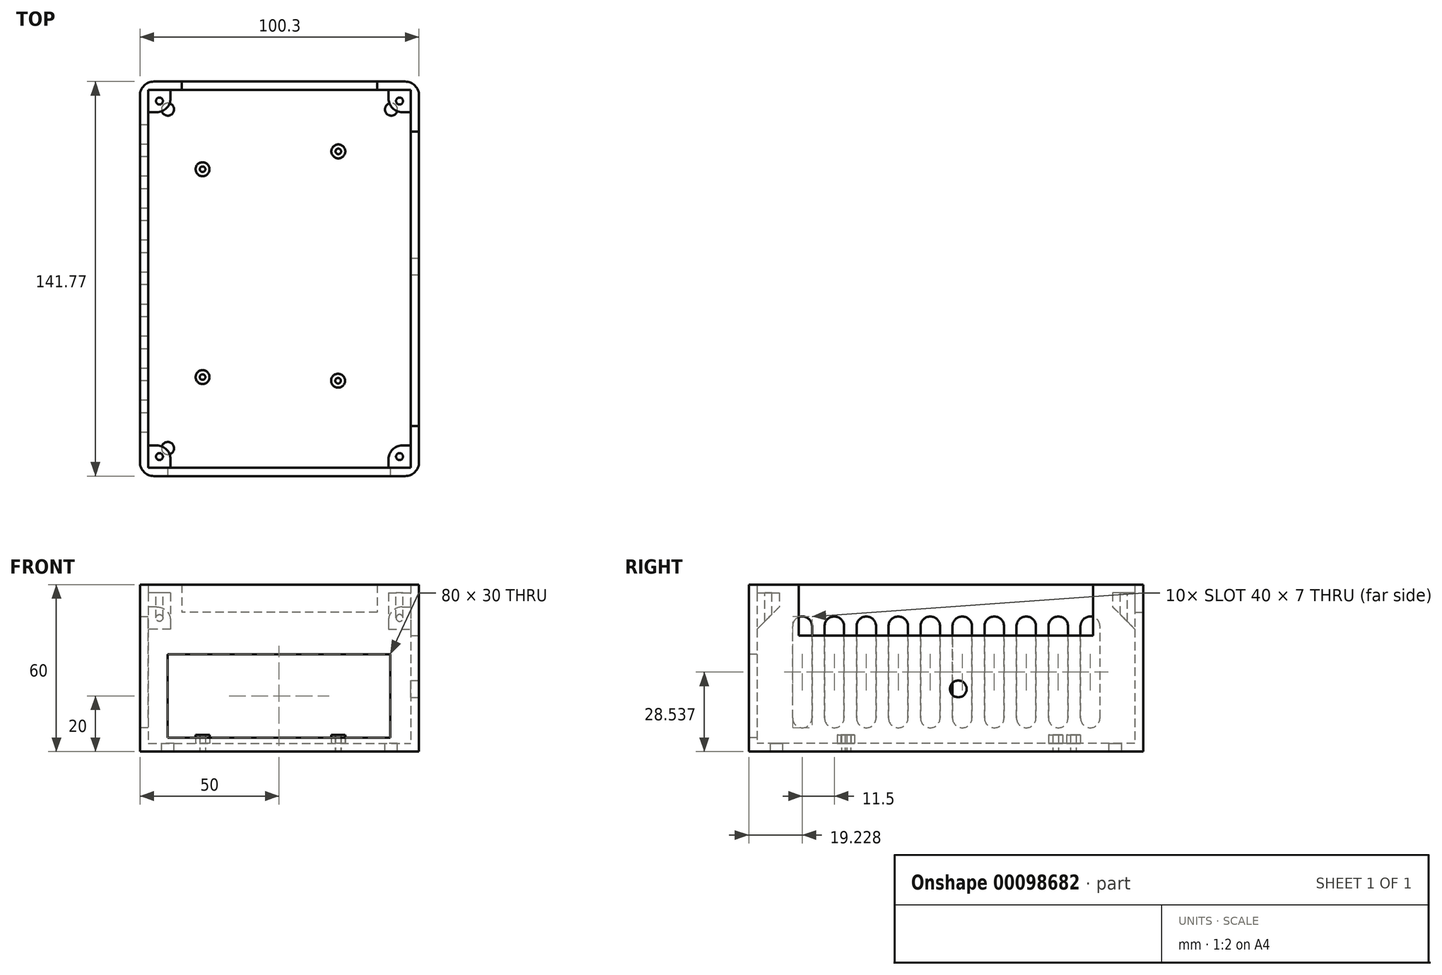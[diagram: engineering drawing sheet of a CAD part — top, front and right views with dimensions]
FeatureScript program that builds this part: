
annotation { "Feature Type Name" : "Feature", "Feature Type Description" : "" }
export const myFeature = defineFeature(function(context is Context, id is Id, definition is map)
    precondition{}
    {
        {
            var Q0;
            Q0=qCreatedBy(makeId("Top.planeOp"),FACE);
            var sketch = newSketch(context, id + "F0", { "sketchPlane" : qUnion([Q0])});
            skLineSegment(sketch, "E0.bottom", {"start": v(-36.7, -58.9) * mm, "end": v(23.6, -58.9) * mm});
            skLineSegment(sketch, "E0.top", {"start": v(-36.7, 42.88) * mm, "end": v(23.6, 42.88) * mm});
            skLineSegment(sketch, "E0.left", {"start": v(-36.7, -58.9) * mm, "end": v(-36.7, 42.88) * mm});
            skLineSegment(sketch, "E0.right", {"start": v(23.6, -58.9) * mm, "end": v(23.6, 42.88) * mm});
            skCircle(sketch, "E1", {"center": v(-34.2, 31.38) * mm, "radius": 2 * mm});
            skCircle(sketch, "E2", {"center": v(14.6, 37.78) * mm, "radius": 2 * mm});
            skCircle(sketch, "E3", {"center": v(-18.03, 7.58) * mm, "radius": 2 * mm});
            skCircle(sketch, "E4", {"center": v(9.3, 7.58) * mm, "radius": 2 * mm});
            skCircle(sketch, "E5", {"center": v(-34.2, -43.32) * mm, "radius": 2 * mm});
            skCircle(sketch, "E6", {"center": v(14.5, -44.62) * mm, "radius": 2 * mm});
            skSolve(sketch);
        }
        {
            var Q0;
            Q0=makeQuery(id+"F0.imprint","IMPRINT",FACE,{"disambiguationData":[TD([[makeQuery(id+"F0.imprint","IMPRINT",EDGE,{"derivedFrom":sQuery(id+"F0.wireOp",EDGE,"E0.bottom")}),1.0]])]});
            var sketch = newSketch(context, id + "F1", { "sketchPlane" : qUnion([Q0])});
            skLineSegment(sketch, "E7.bottom", {"start": v(-56.7, 62.88) * mm, "end": v(43.6, 62.88) * mm});
            skLineSegment(sketch, "E7.top", {"start": v(-56.7, -78.9) * mm, "end": v(43.6, -78.9) * mm});
            skLineSegment(sketch, "E7.left", {"start": v(-56.7, 62.88) * mm, "end": v(-56.7, -78.9) * mm});
            skLineSegment(sketch, "E7.right", {"start": v(43.6, 62.88) * mm, "end": v(43.6, -78.9) * mm});
            skSolve(sketch);
        }
        {
            var Q0;
            Q0 = qSketchRegion(id + "F1", true);
            extrude(context, id + "F2", {"entities" : qUnion([Q0]), "depth" : 60 * mm});
        }
        {
            var Q0;
            Q0=makeQuery(id+"F2.opExtrude","CAP_FACE",FACE,{"disambiguationData":[OSD([sQuery(id+"F1.wireOp",EDGE,"E7.bottom"),sQuery(id+"F1.wireOp",EDGE,"E7.top"),sQuery(id+"F1.wireOp",EDGE,"E7.left"),sQuery(id+"F1.wireOp",EDGE,"E7.right")])],"isStart":false});
            shell(context, id + "F3", {"entities" : qUnion([Q0]), "thickness" : 3 * mm});
        }
        {
            var Q0;
            Q0=makeQuery(id+"F3.opShell","OFFSET_FACE",FACE,{"disambiguationData":[OSD([sQuery(id+"F1.wireOp",EDGE,"E7.bottom"),sQuery(id+"F1.wireOp",EDGE,"E7.top"),sQuery(id+"F1.wireOp",EDGE,"E7.left"),sQuery(id+"F1.wireOp",EDGE,"E7.right")])]});
            var sketch = newSketch(context, id + "F4", { "sketchPlane" : qUnion([Q0])});
            skCircle(sketch, "E8.0", {"center": v(-34.2, 31.38) * mm, "radius": 2 * mm});
            skCircle(sketch, "E9.0", {"center": v(14.6, 37.78) * mm, "radius": 2 * mm});
            skCircle(sketch, "E10.0", {"center": v(-34.2, -43.32) * mm, "radius": 2 * mm});
            skCircle(sketch, "E11.0", {"center": v(14.5, -44.62) * mm, "radius": 2 * mm});
            skSolve(sketch);
        }
        {
            var Q0;
            Q0=makeQuery(id+"F4.imprint","IMPRINT",FACE,{"disambiguationData":[TD([[makeQuery(id+"F4.imprint","IMPRINT",EDGE,{"derivedFrom":sQuery(id+"F4.wireOp",EDGE,"E8.0")}),1.0]])]});
            var Q1;
            Q1=makeQuery(id+"F4.imprint","IMPRINT",FACE,{"disambiguationData":[TD([[makeQuery(id+"F4.imprint","IMPRINT",EDGE,{"derivedFrom":sQuery(id+"F4.wireOp",EDGE,"E9.0")}),1.0]])]});
            var Q2;
            Q2=makeQuery(id+"F4.imprint","IMPRINT",FACE,{"disambiguationData":[TD([[makeQuery(id+"F4.imprint","IMPRINT",EDGE,{"derivedFrom":sQuery(id+"F4.wireOp",EDGE,"E11.0")}),1.0]])]});
            var Q3;
            Q3=makeQuery(id+"F4.imprint","IMPRINT",FACE,{"disambiguationData":[TD([[makeQuery(id+"F4.imprint","IMPRINT",EDGE,{"derivedFrom":sQuery(id+"F4.wireOp",EDGE,"E10.0")}),1.0]])]});
            extrude(context, id + "F5", {"entities" : qUnion([Q0, Q1, Q2, Q3]), "operationType" : NewBodyOperationType.REMOVE, "oppositeDirection" : true, "depth" : 25 * mm});
        }
        {
            var Q0;
            Q0=makeQuery(id+"F2.opExtrude","SWEPT_FACE",FACE,{"disambiguationData":[OSD([sQuery(id+"F1.wireOp",EDGE,"E7.top")])]});
            var sketch = newSketch(context, id + "F6", { "sketchPlane" : qUnion([Q0])});
            skLineSegment(sketch, "E12.bottom", {"start": v(33.3, 5) * mm, "end": v(-46.7, 5) * mm});
            skLineSegment(sketch, "E12.top", {"start": v(33.3, 35) * mm, "end": v(-46.7, 35) * mm});
            skLineSegment(sketch, "E12.left", {"start": v(33.3, 5) * mm, "end": v(33.3, 35) * mm});
            skLineSegment(sketch, "E12.right", {"start": v(-46.7, 5) * mm, "end": v(-46.7, 35) * mm});
            skPoint(sketch, "E12.middle", {"position": v(-6.7, 20) * mm});
            skSolve(sketch);
        }
        {
            var Q0;
            Q0 = qSketchRegion(id + "F6", true);
            extrude(context, id + "F7", {"entities" : qUnion([Q0]), "operationType" : NewBodyOperationType.REMOVE, "oppositeDirection" : true, "depth" : 25 * mm});
        }
        {
            var Q0;
            Q0=makeQuery(id+"F2.opExtrude","SWEPT_FACE",FACE,{"disambiguationData":[OSD([sQuery(id+"F1.wireOp",EDGE,"E7.right")])]});
            var sketch = newSketch(context, id + "F8", { "sketchPlane" : qUnion([Q0])});
            skLineSegment(sketch, "E13.bottom", {"start": v(-60.9, 60) * mm, "end": v(44.88, 60) * mm});
            skLineSegment(sketch, "E13.top", {"start": v(-60.9, 41.64) * mm, "end": v(44.88, 41.64) * mm});
            skLineSegment(sketch, "E13.left", {"start": v(-60.9, 60) * mm, "end": v(-60.9, 41.64) * mm});
            skLineSegment(sketch, "E13.right", {"start": v(44.88, 60) * mm, "end": v(44.88, 41.64) * mm});
            skSolve(sketch);
        }
        {
            var Q0;
            Q0 = qSketchRegion(id + "F8", true);
            extrude(context, id + "F9", {"entities" : qUnion([Q0]), "operationType" : NewBodyOperationType.REMOVE, "oppositeDirection" : true, "depth" : 25 * mm});
        }
        {
            var Q0;
            Q0=makeQuery(id+"F2.opExtrude","SWEPT_FACE",FACE,{"disambiguationData":[OSD([sQuery(id+"F1.wireOp",EDGE,"E7.bottom")])]});
            var sketch = newSketch(context, id + "F10", { "sketchPlane" : qUnion([Q0])});
            skLineSegment(sketch, "E14.bottom", {"start": v(-28.6, 60) * mm, "end": v(41.7, 60) * mm});
            skLineSegment(sketch, "E14.top", {"start": v(-28.6, 50) * mm, "end": v(41.7, 50) * mm});
            skLineSegment(sketch, "E14.left", {"start": v(-28.6, 60) * mm, "end": v(-28.6, 50) * mm});
            skLineSegment(sketch, "E14.right", {"start": v(41.7, 60) * mm, "end": v(41.7, 50) * mm});
            skSolve(sketch);
        }
        {
            var Q0;
            Q0 = qSketchRegion(id + "F10", true);
            extrude(context, id + "F11", {"entities" : qUnion([Q0]), "operationType" : NewBodyOperationType.REMOVE, "oppositeDirection" : true, "depth" : 25 * mm});
        }
        {
            var Q0;
            Q0=makeQuery(id+"F3.opShell","OFFSET_FACE",FACE,{"disambiguationData":[OSD([sQuery(id+"F1.wireOp",EDGE,"E7.bottom"),sQuery(id+"F1.wireOp",EDGE,"E7.top"),sQuery(id+"F1.wireOp",EDGE,"E7.left"),sQuery(id+"F1.wireOp",EDGE,"E7.right")])]});
            var sketch = newSketch(context, id + "F12", { "sketchPlane" : qUnion([Q0])});
            skLineSegment(sketch, "E15.bottom", {"start": v(-46.7, 52.88) * mm, "end": v(33.6, 52.88) * mm, "construction": true});
            skLineSegment(sketch, "E15.top", {"start": v(-46.7, -68.9) * mm, "end": v(33.6, -68.9) * mm, "construction": true});
            skLineSegment(sketch, "E15.left", {"start": v(-46.7, 52.88) * mm, "end": v(-46.7, -68.9) * mm, "construction": true});
            skLineSegment(sketch, "E15.right", {"start": v(33.6, 52.88) * mm, "end": v(33.6, -68.9) * mm, "construction": true});
            skPoint(sketch, "E15.middle", {"position": v(-6.55, -8) * mm});
            skPoint(sketch, "E15.middle.positionSnap0", {"position": v(-53.7, -8) * mm});
            skPoint(sketch, "E15.middle.positionSnap1", {"position": v(-6.55, 59.88) * mm});
            skPoint(sketch, "E15.centerSnap0", {"position": v(-53.7, -8) * mm});
            skPoint(sketch, "E15.centerSnap1", {"position": v(-6.55, 59.88) * mm});
            skCircle(sketch, "E16", {"center": v(-46.7, 52.88) * mm, "radius": 2.25 * mm});
            skCircle(sketch, "E17", {"center": v(33.6, 52.88) * mm, "radius": 2.25 * mm});
            skCircle(sketch, "E18", {"center": v(-46.7, -68.9) * mm, "radius": 2.25 * mm});
            skSolve(sketch);
        }
        {
            var Q0;
            Q0 = qSketchRegion(id + "F12", true);
            extrude(context, id + "F13", {"entities" : qUnion([Q0]), "operationType" : NewBodyOperationType.REMOVE, "oppositeDirection" : true, "depth" : 25 * mm});
        }
        {
            var Q0;
            Q0=makeQuery(id+"F3.opShell","OFFSET_FACE",FACE,{"disambiguationData":[OSD([sQuery(id+"F1.wireOp",EDGE,"E7.left")])]});
            var sketch = newSketch(context, id + "F14", { "sketchPlane" : qUnion([Q0])});
            skLineSegment(sketch, "E19", {"start": v(59.88, 57) * mm, "end": v(51.88, 57) * mm});
            skLineSegment(sketch, "E20", {"start": v(51.88, 57) * mm, "end": v(51.88, 52) * mm});
            skLineSegment(sketch, "E21", {"start": v(51.88, 52) * mm, "end": v(59.88, 44) * mm});
            skLineSegment(sketch, "E22", {"start": v(59.88, 44) * mm, "end": v(59.88, 57) * mm});
            skLineSegment(sketch, "E23", {"start": v(-8, 60) * mm, "end": v(-8, 44.9) * mm});
            skPoint(sketch, "E23.endSnap0", {"position": v(-8, 60) * mm});
            skLineSegment(sketch, "E24.MirrorCS", {"start": v(-75.9, 44) * mm, "end": v(-75.9, 57) * mm});
            skLineSegment(sketch, "E25.MirrorCS", {"start": v(-75.9, 57) * mm, "end": v(-67.9, 57) * mm});
            skLineSegment(sketch, "E26.MirrorCS", {"start": v(-67.9, 52) * mm, "end": v(-75.9, 44) * mm});
            skLineSegment(sketch, "E27.MirrorCS", {"start": v(-67.9, 57) * mm, "end": v(-67.9, 52) * mm});
            skSolve(sketch);
        }
        {
            var Q0;
            Q0 = qSketchRegion(id + "F14", true);
            extrude(context, id + "F15", {"entities" : qUnion([Q0]), "operationType" : NewBodyOperationType.ADD, "depth" : 8 * mm});
        }
        {
            var Q0;
            Q0=makeQuery(id+"F3.opShell","OFFSET_FACE",FACE,{"disambiguationData":[OSD([sQuery(id+"F1.wireOp",EDGE,"E7.right")])]});
            var sketch = newSketch(context, id + "F16", { "sketchPlane" : qUnion([Q0])});
            skLineSegment(sketch, "E28.0.0", {"start": v(-59.88, 44) * mm, "end": v(-59.88, 57) * mm});
            skLineSegment(sketch, "E28.0.1", {"start": v(-59.88, 57) * mm, "end": v(-51.88, 57) * mm});
            skLineSegment(sketch, "E28.0.2", {"start": v(-51.88, 57) * mm, "end": v(-51.88, 52) * mm});
            skLineSegment(sketch, "E28.0.3", {"start": v(-51.88, 52) * mm, "end": v(-59.88, 44) * mm});
            skLineSegment(sketch, "E29.0.0", {"start": v(67.9, 57) * mm, "end": v(75.9, 57) * mm});
            skLineSegment(sketch, "E29.0.1", {"start": v(75.9, 57) * mm, "end": v(75.9, 44) * mm});
            skLineSegment(sketch, "E29.0.2", {"start": v(75.9, 44) * mm, "end": v(67.9, 52) * mm});
            skLineSegment(sketch, "E29.0.3", {"start": v(67.9, 52) * mm, "end": v(67.9, 57) * mm});
            skSolve(sketch);
        }
        {
            var Q0;
            Q0 = qSketchRegion(id + "F16", true);
            extrude(context, id + "F17", {"entities" : qUnion([Q0]), "operationType" : NewBodyOperationType.ADD, "depth" : 8 * mm});
        }
        {
            var Q0;
            Q0=makeQuery(id+"F17.opExtrude","SWEPT_FACE",FACE,{"disambiguationData":[OSD([sQuery(id+"F16.wireOp",EDGE,"E28.0.1")])]});
            var sketch = newSketch(context, id + "F18", { "sketchPlane" : qUnion([Q0])});
            skCircle(sketch, "E30", {"center": v(36.6, 55.88) * mm, "radius": 1.25 * mm});
            skPoint(sketch, "E30.centerSnap0", {"position": v(36.6, 59.88) * mm});
            skPoint(sketch, "E31", {"position": v(32.6, 55.88) * mm});
            skSolve(sketch);
        }
        {
            var Q0;
            Q0=makeQuery(id+"F15.opExtrude","SWEPT_FACE",FACE,{"disambiguationData":[OSD([sQuery(id+"F14.wireOp",EDGE,"E19")])]});
            var sketch = newSketch(context, id + "F19", { "sketchPlane" : qUnion([Q0])});
            skCircle(sketch, "E32", {"center": v(-49.7, 55.88) * mm, "radius": 1.25 * mm});
            skPoint(sketch, "E32.centerSnap0", {"position": v(-45.7, 55.88) * mm});
            skPoint(sketch, "E32.centerSnap1", {"position": v(-49.7, 51.88) * mm});
            skSolve(sketch);
        }
        {
            var Q0;
            Q0=makeQuery(id+"F15.opExtrude","SWEPT_FACE",FACE,{"disambiguationData":[OSD([sQuery(id+"F14.wireOp",EDGE,"E25.MirrorCS")])]});
            var sketch = newSketch(context, id + "F20", { "sketchPlane" : qUnion([Q0])});
            skCircle(sketch, "E33", {"center": v(-49.7, -71.9) * mm, "radius": 1.25 * mm});
            skPoint(sketch, "E33.centerSnap0", {"position": v(-45.7, -71.9) * mm});
            skPoint(sketch, "E33.centerSnap1", {"position": v(-49.7, -67.9) * mm});
            skSolve(sketch);
        }
        {
            var Q0;
            Q0=makeQuery(id+"F17.opExtrude","SWEPT_FACE",FACE,{"disambiguationData":[OSD([sQuery(id+"F16.wireOp",EDGE,"E29.0.0")])]});
            var sketch = newSketch(context, id + "F21", { "sketchPlane" : qUnion([Q0])});
            skCircle(sketch, "E34", {"center": v(36.6, -71.9) * mm, "radius": 1.25 * mm});
            skPoint(sketch, "E34.centerSnap0", {"position": v(32.6, -71.9) * mm});
            skPoint(sketch, "E34.centerSnap1", {"position": v(36.6, -67.9) * mm});
            skSolve(sketch);
        }
        {
            var Q0;
            Q0=makeQuery(id+"F19.imprint","IMPRINT",FACE,{"disambiguationData":[TD([[makeQuery(id+"F19.imprint","IMPRINT",EDGE,{"derivedFrom":sQuery(id+"F19.wireOp",EDGE,"E32")}),1.0]])]});
            var Q1;
            Q1=makeQuery(id+"F18.imprint","IMPRINT",FACE,{"disambiguationData":[TD([[makeQuery(id+"F18.imprint","IMPRINT",EDGE,{"derivedFrom":sQuery(id+"F18.wireOp",EDGE,"E30")}),1.0]])]});
            var Q2;
            Q2=makeQuery(id+"F20.imprint","IMPRINT",FACE,{"disambiguationData":[TD([[makeQuery(id+"F20.imprint","IMPRINT",EDGE,{"derivedFrom":sQuery(id+"F20.wireOp",EDGE,"E33")}),1.0]])]});
            var Q3;
            Q3=makeQuery(id+"F21.imprint","IMPRINT",FACE,{"disambiguationData":[TD([[makeQuery(id+"F21.imprint","IMPRINT",EDGE,{"derivedFrom":sQuery(id+"F21.wireOp",EDGE,"E34")}),1.0]])]});
            var Q4;
            Q4=sQuery(id+"F19.wireOp",EDGE,"E32");
            var Q5;
            Q5=sQuery(id+"F18.wireOp",EDGE,"E30");
            var Q6;
            Q6=sQuery(id+"F20.wireOp",EDGE,"E33");
            var Q7;
            Q7=sQuery(id+"F21.wireOp",EDGE,"E34");
            extrude(context, id + "F22", {"entities" : qUnion([Q0, Q1, Q2, Q3]), "operationType" : NewBodyOperationType.REMOVE, "surfaceEntities" : qUnion([Q4, Q5, Q6, Q7]), "oppositeDirection" : true, "depth" : 25 * mm});
        }
        {
            var Q0;
            Q0=makeQuery(id+"F15.opExtrude","CAP_EDGE",EDGE,{"disambiguationData":[OSD([sQuery(id+"F14.wireOp",EDGE,"E20")])],"isStart":false});
            var Q1;
            Q1=makeQuery(id+"F17.opExtrude","CAP_EDGE",EDGE,{"disambiguationData":[OSD([sQuery(id+"F16.wireOp",EDGE,"E28.0.2")])],"isStart":false});
            var Q2;
            Q2=makeQuery(id+"F15.opExtrude","CAP_EDGE",EDGE,{"disambiguationData":[OSD([sQuery(id+"F14.wireOp",EDGE,"E27.MirrorCS")])],"isStart":false});
            var Q3;
            Q3=makeQuery(id+"F17.opExtrude","CAP_EDGE",EDGE,{"disambiguationData":[OSD([sQuery(id+"F16.wireOp",EDGE,"E29.0.3")])],"isStart":false});
            fillet(context, id + "F23", {"entities" : qUnion([Q0, Q1, Q2, Q3]), "radius" : 5 * mm, "tangentPropagation" : true, "allowEdgeOverflow" : false});
        }
        {
            var Q0;
            Q0=makeQuery(id+"F2.opExtrude","SWEPT_EDGE",EDGE,{"disambiguationData":[OSD([sQuery(id+"F1.wireOp",EDGE,"E7.bottom"),sQuery(id+"F1.wireOp",EDGE,"E7.right")])]});
            var Q1;
            Q1=makeQuery(id+"F2.opExtrude","SWEPT_EDGE",EDGE,{"disambiguationData":[OSD([sQuery(id+"F1.wireOp",EDGE,"E7.bottom"),sQuery(id+"F1.wireOp",EDGE,"E7.left")])]});
            var Q2;
            Q2=makeQuery(id+"F2.opExtrude","SWEPT_EDGE",EDGE,{"disambiguationData":[OSD([sQuery(id+"F1.wireOp",EDGE,"E7.top"),sQuery(id+"F1.wireOp",EDGE,"E7.left")])]});
            var Q3;
            Q3=makeQuery(id+"F2.opExtrude","SWEPT_EDGE",EDGE,{"disambiguationData":[OSD([sQuery(id+"F1.wireOp",EDGE,"E7.top"),sQuery(id+"F1.wireOp",EDGE,"E7.right")])]});
            fillet(context, id + "F24", {"entities" : qUnion([Q0, Q1, Q2, Q3]), "radius" : 5 * mm, "tangentPropagation" : true, "allowEdgeOverflow" : false});
        }
        {
            var Q0;
            Q0=makeQuery(id+"F2.opExtrude","SWEPT_FACE",FACE,{"disambiguationData":[OSD([sQuery(id+"F1.wireOp",EDGE,"E7.right")])]});
            var sketch = newSketch(context, id + "F25", { "sketchPlane" : qUnion([Q0])});
            skCircle(sketch, "E35", {"center": v(-3.57, 22.5) * mm, "radius": 3 * mm});
            skSolve(sketch);
        }
        {
            var Q0;
            Q0 = qSketchRegion(id + "F25", true);
            extrude(context, id + "F26", {"entities" : qUnion([Q0]), "operationType" : NewBodyOperationType.REMOVE, "oppositeDirection" : true, "depth" : 25 * mm});
        }
        {
            var Q0;
            Q0=makeQuery(id+"F2.opExtrude","SWEPT_FACE",FACE,{"disambiguationData":[OSD([sQuery(id+"F1.wireOp",EDGE,"E7.left")])]});
            var sketch = newSketch(context, id + "F27", { "sketchPlane" : qUnion([Q0])});
            skLineSegment(sketch, "E36.bottom", {"start": v(-47.34, 48.54) * mm, "end": v(-40.34, 48.54) * mm});
            skLineSegment(sketch, "E36.top", {"start": v(-47.34, 8.54) * mm, "end": v(-40.34, 8.54) * mm});
            skLineSegment(sketch, "E36.left", {"start": v(-47.34, 48.54) * mm, "end": v(-47.34, 8.54) * mm});
            skLineSegment(sketch, "E36.right", {"start": v(-40.34, 48.54) * mm, "end": v(-40.34, 8.54) * mm});
            skPoint(sketch, "E37.firstSnap0", {"position": v(-43.84, 48.54) * mm});
            skLineSegment(sketch, "E38.1.0.0", {"start": v(-22.34, 48.54) * mm, "end": v(-15.34, 48.54) * mm});
            skLineSegment(sketch, "E38.1.0.1", {"start": v(-15.34, 48.54) * mm, "end": v(-15.34, 8.54) * mm});
            skLineSegment(sketch, "E38.1.0.2", {"start": v(-22.34, 48.54) * mm, "end": v(-22.34, 8.54) * mm});
            skLineSegment(sketch, "E38.2.0.0", {"start": v(2.66, 48.54) * mm, "end": v(9.66, 48.54) * mm});
            skLineSegment(sketch, "E38.2.0.1", {"start": v(9.66, 48.54) * mm, "end": v(9.66, 8.54) * mm});
            skLineSegment(sketch, "E38.2.0.2", {"start": v(2.66, 48.54) * mm, "end": v(2.66, 8.54) * mm});
            skLineSegment(sketch, "E38.direction1", {"start": v(-47.34, 48.54) * mm, "end": v(-22.34, 48.54) * mm, "construction": true});
            skSolve(sketch);
        }
        {
            var Q0;
            Q0 = qSketchRegion(id + "F27", true);
            extrude(context, id + "F28", {"entities" : qUnion([Q0]), "operationType" : NewBodyOperationType.REMOVE, "oppositeDirection" : true, "depth" : 25 * mm});
        }
        {
            var Q0;
            Q0=makeQuery(id+"F28.boolean.opBoolean","COPY",EDGE,{"derivedFrom":makeQuery(id+"F28.opExtrude","SWEPT_EDGE",EDGE,{"disambiguationData":[OSD([sQuery(id+"F27.wireOp",EDGE,"E36.bottom"),sQuery(id+"F27.wireOp",EDGE,"E36.right")])]})});
            var Q1;
            Q1=makeQuery(id+"F28.boolean.opBoolean","COPY",EDGE,{"derivedFrom":makeQuery(id+"F28.opExtrude","SWEPT_EDGE",EDGE,{"disambiguationData":[OSD([sQuery(id+"F27.wireOp",EDGE,"E36.bottom"),sQuery(id+"F27.wireOp",EDGE,"E36.left")])]})});
            var Q2;
            Q2=makeQuery(id+"F28.boolean.opBoolean","COPY",EDGE,{"derivedFrom":makeQuery(id+"F28.opExtrude","SWEPT_EDGE",EDGE,{"disambiguationData":[OSD([sQuery(id+"F27.wireOp",EDGE,"E36.top"),sQuery(id+"F27.wireOp",EDGE,"E36.right")])]})});
            var Q3;
            Q3=makeQuery(id+"F28.boolean.opBoolean","COPY",EDGE,{"derivedFrom":makeQuery(id+"F28.opExtrude","SWEPT_EDGE",EDGE,{"disambiguationData":[OSD([sQuery(id+"F27.wireOp",EDGE,"E36.top"),sQuery(id+"F27.wireOp",EDGE,"E36.left")])]})});
            fillet(context, id + "F29", {"entities" : qUnion([Q0, Q1, Q2, Q3]), "radius" : 3.5 * mm, "tangentPropagation" : true, "allowEdgeOverflow" : false});
        }
        {
            var Q0;
            Q0=makeQuery(id+"F2.opExtrude","SWEPT_FACE",FACE,{"disambiguationData":[OSD([sQuery(id+"F1.wireOp",EDGE,"E7.left")])]});
            var sketch = newSketch(context, id + "F30", { "sketchPlane" : qUnion([Q0])});
            skLineSegment(sketch, "E39.0", {"start": v(-40.34, 45.04) * mm, "end": v(-40.34, 12.04) * mm});
            skArc(sketch, "E40.1", {"start": v(-47.34, 45.04) * mm, "mid": v(-43.84, 48.54) * mm, "end": v(-40.34, 45.04) * mm});
            skLineSegment(sketch, "E41.0", {"start": v(-47.34, 45.04) * mm, "end": v(-47.34, 12.04) * mm});
            skArc(sketch, "E42.0", {"start": v(-40.34, 12.04) * mm, "mid": v(-43.84, 8.54) * mm, "end": v(-47.34, 12.04) * mm});
            skLineSegment(sketch, "E43.1.0.0", {"start": v(-28.84, 45.04) * mm, "end": v(-28.84, 12.04) * mm});
            skArc(sketch, "E43.1.0.1", {"start": v(-35.84, 45.04) * mm, "mid": v(-32.34, 48.54) * mm, "end": v(-28.84, 45.04) * mm});
            skLineSegment(sketch, "E43.1.0.2", {"start": v(-35.84, 45.04) * mm, "end": v(-35.84, 12.04) * mm});
            skArc(sketch, "E43.1.0.3", {"start": v(-28.84, 12.04) * mm, "mid": v(-32.34, 8.54) * mm, "end": v(-35.84, 12.04) * mm});
            skLineSegment(sketch, "E43.2.0.0", {"start": v(-17.34, 45.04) * mm, "end": v(-17.34, 12.04) * mm});
            skArc(sketch, "E43.2.0.1", {"start": v(-24.34, 45.04) * mm, "mid": v(-20.84, 48.54) * mm, "end": v(-17.34, 45.04) * mm});
            skLineSegment(sketch, "E43.2.0.2", {"start": v(-24.34, 45.04) * mm, "end": v(-24.34, 12.04) * mm});
            skArc(sketch, "E43.2.0.3", {"start": v(-17.34, 12.04) * mm, "mid": v(-20.84, 8.54) * mm, "end": v(-24.34, 12.04) * mm});
            skLineSegment(sketch, "E43.3.0.0", {"start": v(-5.84, 45.04) * mm, "end": v(-5.84, 12.04) * mm});
            skArc(sketch, "E43.3.0.1", {"start": v(-12.84, 45.04) * mm, "mid": v(-9.34, 48.54) * mm, "end": v(-5.84, 45.04) * mm});
            skLineSegment(sketch, "E43.3.0.2", {"start": v(-12.84, 45.04) * mm, "end": v(-12.84, 12.04) * mm});
            skArc(sketch, "E43.3.0.3", {"start": v(-5.84, 12.04) * mm, "mid": v(-9.34, 8.54) * mm, "end": v(-12.84, 12.04) * mm});
            skLineSegment(sketch, "E43.4.0.0", {"start": v(5.66, 45.04) * mm, "end": v(5.66, 12.04) * mm});
            skArc(sketch, "E43.4.0.1", {"start": v(-1.34, 45.04) * mm, "mid": v(2.16, 48.54) * mm, "end": v(5.66, 45.04) * mm});
            skLineSegment(sketch, "E43.4.0.2", {"start": v(-1.34, 45.04) * mm, "end": v(-1.34, 12.04) * mm});
            skArc(sketch, "E43.4.0.3", {"start": v(5.66, 12.04) * mm, "mid": v(2.16, 8.54) * mm, "end": v(-1.34, 12.04) * mm});
            skLineSegment(sketch, "E43.5.0.0", {"start": v(17.16, 45.04) * mm, "end": v(17.16, 12.04) * mm});
            skArc(sketch, "E43.5.0.1", {"start": v(10.16, 45.04) * mm, "mid": v(13.66, 48.54) * mm, "end": v(17.16, 45.04) * mm});
            skLineSegment(sketch, "E43.5.0.2", {"start": v(10.16, 45.04) * mm, "end": v(10.16, 12.04) * mm});
            skArc(sketch, "E43.5.0.3", {"start": v(17.16, 12.04) * mm, "mid": v(13.66, 8.54) * mm, "end": v(10.16, 12.04) * mm});
            skLineSegment(sketch, "E43.6.0.0", {"start": v(28.66, 45.04) * mm, "end": v(28.66, 12.04) * mm});
            skArc(sketch, "E43.6.0.1", {"start": v(21.66, 45.04) * mm, "mid": v(25.16, 48.54) * mm, "end": v(28.66, 45.04) * mm});
            skLineSegment(sketch, "E43.6.0.2", {"start": v(21.66, 45.04) * mm, "end": v(21.66, 12.04) * mm});
            skArc(sketch, "E43.6.0.3", {"start": v(28.66, 12.04) * mm, "mid": v(25.16, 8.54) * mm, "end": v(21.66, 12.04) * mm});
            skLineSegment(sketch, "E43.7.0.0", {"start": v(40.16, 45.04) * mm, "end": v(40.16, 12.04) * mm});
            skArc(sketch, "E43.7.0.1", {"start": v(33.16, 45.04) * mm, "mid": v(36.66, 48.54) * mm, "end": v(40.16, 45.04) * mm});
            skLineSegment(sketch, "E43.7.0.2", {"start": v(33.16, 45.04) * mm, "end": v(33.16, 12.04) * mm});
            skArc(sketch, "E43.7.0.3", {"start": v(40.16, 12.04) * mm, "mid": v(36.66, 8.54) * mm, "end": v(33.16, 12.04) * mm});
            skLineSegment(sketch, "E43.8.0.0", {"start": v(51.66, 45.04) * mm, "end": v(51.66, 12.04) * mm});
            skArc(sketch, "E43.8.0.1", {"start": v(44.66, 45.04) * mm, "mid": v(48.16, 48.54) * mm, "end": v(51.66, 45.04) * mm});
            skLineSegment(sketch, "E43.8.0.2", {"start": v(44.66, 45.04) * mm, "end": v(44.66, 12.04) * mm});
            skArc(sketch, "E43.8.0.3", {"start": v(51.66, 12.04) * mm, "mid": v(48.16, 8.54) * mm, "end": v(44.66, 12.04) * mm});
            skLineSegment(sketch, "E43.9.0.0", {"start": v(63.16, 45.04) * mm, "end": v(63.16, 12.04) * mm});
            skArc(sketch, "E43.9.0.1", {"start": v(56.16, 45.04) * mm, "mid": v(59.66, 48.54) * mm, "end": v(63.16, 45.04) * mm});
            skLineSegment(sketch, "E43.9.0.2", {"start": v(56.16, 45.04) * mm, "end": v(56.16, 12.04) * mm});
            skArc(sketch, "E43.9.0.3", {"start": v(63.16, 12.04) * mm, "mid": v(59.66, 8.54) * mm, "end": v(56.16, 12.04) * mm});
            skLineSegment(sketch, "E43.direction1", {"start": v(-40.34, 12.04) * mm, "end": v(-28.84, 12.04) * mm, "construction": true});
            skSolve(sketch);
        }
        {
            var Q0;
            Q0 = qSketchRegion(id + "F30", true);
            extrude(context, id + "F31", {"entities" : qUnion([Q0]), "operationType" : NewBodyOperationType.REMOVE, "oppositeDirection" : true, "depth" : 25 * mm});
        }
        {
            var Q0;
            Q0=makeQuery(id+"F3.opShell","OFFSET_FACE",FACE,{"disambiguationData":[OSD([sQuery(id+"F1.wireOp",EDGE,"E7.bottom"),sQuery(id+"F1.wireOp",EDGE,"E7.top"),sQuery(id+"F1.wireOp",EDGE,"E7.left"),sQuery(id+"F1.wireOp",EDGE,"E7.right")])]});
            var sketch = newSketch(context, id + "F32", { "sketchPlane" : qUnion([Q0])});
            skCircle(sketch, "E44", {"center": v(-34.2, 31.38) * mm, "radius": 1 * mm});
            skCircle(sketch, "E45", {"center": v(14.6, 37.78) * mm, "radius": 2.5 * mm});
            skCircle(sketch, "E46", {"center": v(14.5, -44.62) * mm, "radius": 1 * mm});
            skCircle(sketch, "E47", {"center": v(14.5, -44.62) * mm, "radius": 2.5 * mm});
            skCircle(sketch, "E48", {"center": v(-34.2, -43.32) * mm, "radius": 1 * mm});
            skCircle(sketch, "E49", {"center": v(-34.2, -43.32) * mm, "radius": 2.5 * mm});
            skCircle(sketch, "E50", {"center": v(14.6, 37.78) * mm, "radius": 1 * mm});
            skCircle(sketch, "E51", {"center": v(-34.2, 31.38) * mm, "radius": 2.5 * mm});
            skSolve(sketch);
        }
        {
            var Q0;
            Q0 = qSketchRegion(id + "F32", true);
            extrude(context, id + "F33", {"entities" : qUnion([Q0]), "operationType" : NewBodyOperationType.ADD, "depth" : 3 * mm, "hasSecondDirection" : true, "secondDirectionOppositeDirection" : true, "secondDirectionDepth" : 3 * mm});
        }
    });
